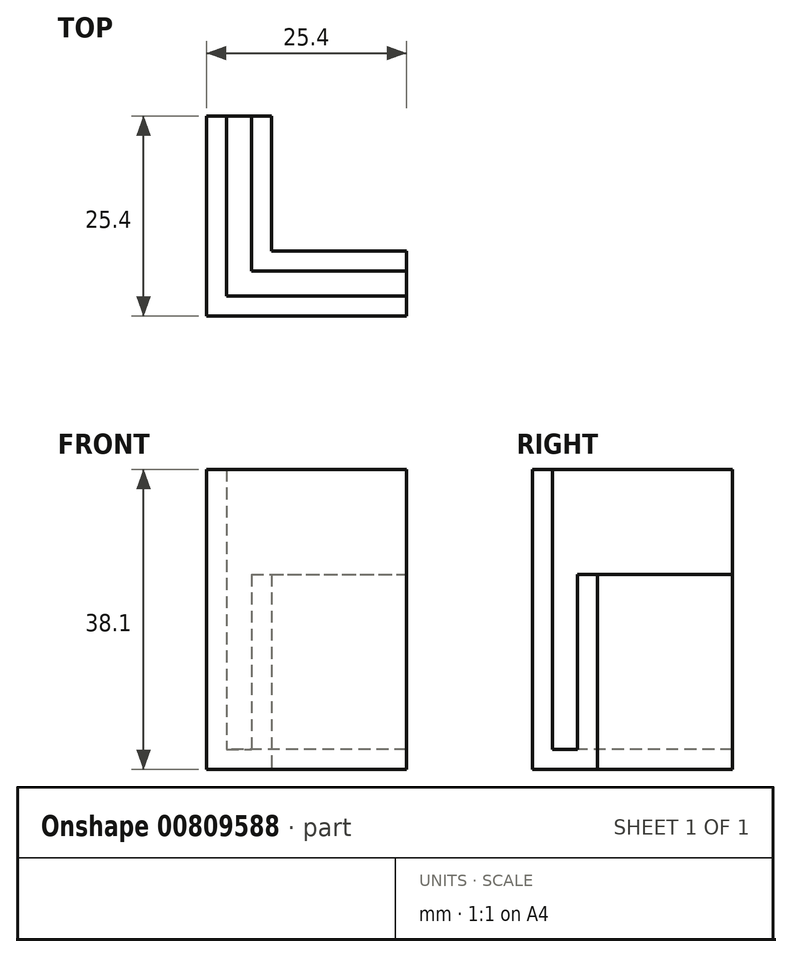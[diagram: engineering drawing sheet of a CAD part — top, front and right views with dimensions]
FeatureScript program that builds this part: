
annotation { "Feature Type Name" : "Feature", "Feature Type Description" : "" }
export const myFeature = defineFeature(function(context is Context, id is Id, definition is map)
    precondition{}
    {
        {
            var Q0;
            Q0=qCreatedBy(makeId("Top.planeOp"),FACE);
            var sketch = newSketch(context, id + "F0", { "sketchPlane" : qUnion([Q0])});
            skLineSegment(sketch, "E0.bottom", {"start": v(0, 0) * mm, "end": v(2.54, 0) * mm});
            skLineSegment(sketch, "E0.top", {"start": v(0, 25.4) * mm, "end": v(2.54, 25.4) * mm});
            skLineSegment(sketch, "E0.left", {"start": v(0, 0) * mm, "end": v(0, 25.4) * mm});
            skLineSegment(sketch, "E0.right", {"start": v(2.54, 0) * mm, "end": v(2.54, 25.4) * mm});
            skLineSegment(sketch, "E1.bottom", {"start": v(0, 0) * mm, "end": v(25.4, 0) * mm});
            skLineSegment(sketch, "E1.top", {"start": v(0, 2.54) * mm, "end": v(25.4, 2.54) * mm});
            skLineSegment(sketch, "E1.left", {"start": v(0, 0) * mm, "end": v(0, 2.54) * mm});
            skLineSegment(sketch, "E1.right", {"start": v(25.4, 0) * mm, "end": v(25.4, 2.54) * mm});
            skLineSegment(sketch, "E2.bottom", {"start": v(0, 0) * mm, "end": v(5.72, 0) * mm});
            skLineSegment(sketch, "E2.top", {"start": v(0, 25.4) * mm, "end": v(5.71, 25.4) * mm});
            skLineSegment(sketch, "E2.right", {"start": v(5.72, 0) * mm, "end": v(5.71, 25.4) * mm});
            skLineSegment(sketch, "E3.bottom", {"start": v(0, 0) * mm, "end": v(8.25, 0) * mm});
            skLineSegment(sketch, "E3.top", {"start": v(0, 25.4) * mm, "end": v(8.25, 25.4) * mm});
            skLineSegment(sketch, "E3.right", {"start": v(8.26, 0) * mm, "end": v(8.25, 25.4) * mm});
            skLineSegment(sketch, "E4.top", {"start": v(0, 5.71) * mm, "end": v(25.4, 5.71) * mm});
            skLineSegment(sketch, "E4.left", {"start": v(0, 0) * mm, "end": v(0, 5.71) * mm});
            skLineSegment(sketch, "E4.right", {"start": v(25.4, 0) * mm, "end": v(25.4, 5.71) * mm});
            skLineSegment(sketch, "E5.top", {"start": v(0, 8.25) * mm, "end": v(25.4, 8.25) * mm});
            skLineSegment(sketch, "E5.left", {"start": v(0, 0) * mm, "end": v(0, 8.25) * mm});
            skLineSegment(sketch, "E5.right", {"start": v(25.4, 0) * mm, "end": v(25.4, 8.25) * mm});
            skSolve(sketch);
        }
        {
            var Q0;
            {var subQ0=sQuery(id+"F0.wireOp",EDGE,"E0.top");Q0=makeQuery(id+"F0.imprint","IMPRINT",FACE,{"disambiguationData":[TD([[makeQuery(id+"F0.imprint","IMPRINT",EDGE,{"derivedFrom":subQ0}),-1.0]])]});}
            var Q1;
            {var subQ0=sQuery(id+"F0.wireOp",EDGE,"E2.top");Q1=makeQuery(id+"F0.imprint","IMPRINT",FACE,{"disambiguationData":[TD([[makeQuery(id+"F0.imprint","IMPRINT",EDGE,{"derivedFrom":subQ0}),-1.0]])]});}
            var Q2;
            {var subQ0=sQuery(id+"F0.wireOp",EDGE,"E3.top");Q2=makeQuery(id+"F0.imprint","IMPRINT",FACE,{"disambiguationData":[TD([[makeQuery(id+"F0.imprint","IMPRINT",EDGE,{"derivedFrom":subQ0}),-1.0]])]});}
            var Q3;
            {var subQ0=sQuery(id+"F0.wireOp",EDGE,"E5.top");var subQ1=sQuery(id+"F0.wireOp",EDGE,"E0.left");var subQ2=makeQuery(id+"F0.imprint","INTERSECT",VERTEX,{"derivedFrom":[subQ1,subQ0]});Q3=makeQuery(id+"F0.imprint","IMPRINT",FACE,{"disambiguationData":[TD([[makeQuery(id+"F0.imprint","IMPRINT",EDGE,{"disambiguationData":[TD([[subQ2,1.0]])],"derivedFrom":subQ1}),-1.0]])]});}
            var Q4;
            {var subQ0=sQuery(id+"F0.wireOp",EDGE,"E1.top");var subQ1=sQuery(id+"F0.wireOp",EDGE,"E0.left");var subQ2=makeQuery(id+"F0.imprint","INTERSECT",VERTEX,{"derivedFrom":[subQ1,subQ0]});Q4=makeQuery(id+"F0.imprint","IMPRINT",FACE,{"disambiguationData":[TD([[makeQuery(id+"F0.imprint","IMPRINT",EDGE,{"disambiguationData":[TD([[subQ2,-1.0]])],"derivedFrom":subQ1}),-1.0]])]});}
            var Q5;
            {var subQ0=sQuery(id+"F0.wireOp",EDGE,"E0.bottom");Q5=makeQuery(id+"F0.imprint","IMPRINT",FACE,{"disambiguationData":[TD([[makeQuery(id+"F0.imprint","IMPRINT",EDGE,{"derivedFrom":subQ0}),1.0]])]});}
            var Q6;
            {var subQ1=sQuery(id+"F0.wireOp",EDGE,"E0.right");var subQ3=sQuery(id+"F0.wireOp",EDGE,"E1.top");var subQ4=makeQuery(id+"F0.imprint","INTERSECT",VERTEX,{"derivedFrom":[subQ1,subQ3]});Q6=makeQuery(id+"F0.imprint","IMPRINT",FACE,{"disambiguationData":[TD([[makeQuery(id+"F0.imprint","IMPRINT",EDGE,{"disambiguationData":[TD([[subQ4,-1.0]])],"derivedFrom":subQ3}),-1.0]])]});}
            var Q7;
            {var subQ0=sQuery(id+"F0.wireOp",EDGE,"E1.top");var subQ1=sQuery(id+"F0.wireOp",EDGE,"E0.right");var subQ2=makeQuery(id+"F0.imprint","INTERSECT",VERTEX,{"derivedFrom":[subQ1,subQ0]});Q7=makeQuery(id+"F0.imprint","IMPRINT",FACE,{"disambiguationData":[TD([[makeQuery(id+"F0.imprint","IMPRINT",EDGE,{"disambiguationData":[TD([[subQ2,-1.0]])],"derivedFrom":subQ1}),-1.0]])]});}
            var Q8;
            {var subQ0=sQuery(id+"F0.wireOp",EDGE,"E5.top");var subQ1=sQuery(id+"F0.wireOp",EDGE,"E0.right");var subQ2=makeQuery(id+"F0.imprint","INTERSECT",VERTEX,{"derivedFrom":[subQ1,subQ0]});Q8=makeQuery(id+"F0.imprint","IMPRINT",FACE,{"disambiguationData":[TD([[makeQuery(id+"F0.imprint","IMPRINT",EDGE,{"disambiguationData":[TD([[subQ2,1.0]])],"derivedFrom":subQ1}),-1.0]])]});}
            var Q9;
            {var subQ0=sQuery(id+"F0.wireOp",EDGE,"E3.right");var subQ1=sQuery(id+"F0.wireOp",EDGE,"E1.top");var subQ2=makeQuery(id+"F0.imprint","INTERSECT",VERTEX,{"derivedFrom":[subQ1,subQ0]});Q9=makeQuery(id+"F0.imprint","IMPRINT",FACE,{"disambiguationData":[TD([[makeQuery(id+"F0.imprint","IMPRINT",EDGE,{"disambiguationData":[TD([[subQ2,1.0]])],"derivedFrom":subQ1}),1.0]])]});}
            var Q10;
            {var subQ0=sQuery(id+"F0.wireOp",EDGE,"E5.top");var subQ1=sQuery(id+"F0.wireOp",EDGE,"E2.right");var subQ2=makeQuery(id+"F0.imprint","INTERSECT",VERTEX,{"derivedFrom":[subQ1,subQ0]});Q10=makeQuery(id+"F0.imprint","IMPRINT",FACE,{"disambiguationData":[TD([[makeQuery(id+"F0.imprint","IMPRINT",EDGE,{"disambiguationData":[TD([[subQ2,1.0]])],"derivedFrom":subQ1}),-1.0]])]});}
            var Q11;
            {var subQ0=sQuery(id+"F0.wireOp",EDGE,"E3.right");var subQ1=sQuery(id+"F0.wireOp",EDGE,"E1.bottom");var subQ2=makeQuery(id+"F0.imprint","INTERSECT",VERTEX,{"derivedFrom":[subQ1,subQ0]});Q11=makeQuery(id+"F0.imprint","IMPRINT",FACE,{"disambiguationData":[TD([[makeQuery(id+"F0.imprint","IMPRINT",EDGE,{"disambiguationData":[TD([[subQ2,1.0]])],"derivedFrom":subQ1}),1.0]])]});}
            var Q12;
            {var subQ3=sQuery(id+"F0.wireOp",EDGE,"E1.right");Q12=makeQuery(id+"F0.imprint","IMPRINT",FACE,{"disambiguationData":[TD([[makeQuery(id+"F0.imprint","IMPRINT",EDGE,{"derivedFrom":subQ3}),1.0]])]});}
            var Q13;
            {var subQ3=sQuery(id+"F0.wireOp",EDGE,"E4.right");Q13=makeQuery(id+"F0.imprint","IMPRINT",FACE,{"disambiguationData":[TD([[makeQuery(id+"F0.imprint","IMPRINT",EDGE,{"derivedFrom":subQ3}),1.0]])]});}
            var Q14;
            {var subQ5=sQuery(id+"F0.wireOp",EDGE,"E5.right");Q14=makeQuery(id+"F0.imprint","IMPRINT",FACE,{"disambiguationData":[TD([[makeQuery(id+"F0.imprint","IMPRINT",EDGE,{"derivedFrom":subQ5}),1.0]])]});}
            extrude(context, id + "F1", {"entities" : qUnion([Q0, Q1, Q2, Q3, Q4, Q5, Q6, Q7, Q8, Q9, Q10, Q11, Q12, Q13, Q14]), "depth" : 2.54 * mm, "offsetDistance" : 25.4 * mm});
        }
        {
            var Q0;
            {var subQ0=sQuery(id+"F0.wireOp",EDGE,"E3.top");Q0=makeQuery(id+"F0.imprint","IMPRINT",FACE,{"disambiguationData":[TD([[makeQuery(id+"F0.imprint","IMPRINT",EDGE,{"derivedFrom":subQ0}),-1.0]])]});}
            var Q1;
            {var subQ0=sQuery(id+"F0.wireOp",EDGE,"E5.top");var subQ1=sQuery(id+"F0.wireOp",EDGE,"E2.right");var subQ2=makeQuery(id+"F0.imprint","INTERSECT",VERTEX,{"derivedFrom":[subQ1,subQ0]});Q1=makeQuery(id+"F0.imprint","IMPRINT",FACE,{"disambiguationData":[TD([[makeQuery(id+"F0.imprint","IMPRINT",EDGE,{"disambiguationData":[TD([[subQ2,1.0]])],"derivedFrom":subQ1}),-1.0]])]});}
            var Q2;
            {var subQ5=sQuery(id+"F0.wireOp",EDGE,"E5.right");Q2=makeQuery(id+"F0.imprint","IMPRINT",FACE,{"disambiguationData":[TD([[makeQuery(id+"F0.imprint","IMPRINT",EDGE,{"derivedFrom":subQ5}),1.0]])]});}
            extrude(context, id + "F2", {"entities" : qUnion([Q0, Q1, Q2]), "operationType" : NewBodyOperationType.ADD, "depth" : 24.77 * mm, "offsetDistance" : 25.4 * mm});
        }
        {
            var Q0;
            {var subQ0=sQuery(id+"F0.wireOp",EDGE,"E0.top");Q0=makeQuery(id+"F0.imprint","IMPRINT",FACE,{"disambiguationData":[TD([[makeQuery(id+"F0.imprint","IMPRINT",EDGE,{"derivedFrom":subQ0}),-1.0]])]});}
            var Q1;
            {var subQ0=sQuery(id+"F0.wireOp",EDGE,"E5.top");var subQ1=sQuery(id+"F0.wireOp",EDGE,"E0.left");var subQ2=makeQuery(id+"F0.imprint","INTERSECT",VERTEX,{"derivedFrom":[subQ1,subQ0]});Q1=makeQuery(id+"F0.imprint","IMPRINT",FACE,{"disambiguationData":[TD([[makeQuery(id+"F0.imprint","IMPRINT",EDGE,{"disambiguationData":[TD([[subQ2,1.0]])],"derivedFrom":subQ1}),-1.0]])]});}
            var Q2;
            {var subQ0=sQuery(id+"F0.wireOp",EDGE,"E1.top");var subQ1=sQuery(id+"F0.wireOp",EDGE,"E0.left");var subQ2=makeQuery(id+"F0.imprint","INTERSECT",VERTEX,{"derivedFrom":[subQ1,subQ0]});Q2=makeQuery(id+"F0.imprint","IMPRINT",FACE,{"disambiguationData":[TD([[makeQuery(id+"F0.imprint","IMPRINT",EDGE,{"disambiguationData":[TD([[subQ2,-1.0]])],"derivedFrom":subQ1}),-1.0]])]});}
            var Q3;
            {var subQ0=sQuery(id+"F0.wireOp",EDGE,"E0.bottom");Q3=makeQuery(id+"F0.imprint","IMPRINT",FACE,{"disambiguationData":[TD([[makeQuery(id+"F0.imprint","IMPRINT",EDGE,{"derivedFrom":subQ0}),1.0]])]});}
            var Q4;
            {var subQ1=sQuery(id+"F0.wireOp",EDGE,"E0.right");var subQ3=sQuery(id+"F0.wireOp",EDGE,"E1.top");var subQ4=makeQuery(id+"F0.imprint","INTERSECT",VERTEX,{"derivedFrom":[subQ1,subQ3]});Q4=makeQuery(id+"F0.imprint","IMPRINT",FACE,{"disambiguationData":[TD([[makeQuery(id+"F0.imprint","IMPRINT",EDGE,{"disambiguationData":[TD([[subQ4,-1.0]])],"derivedFrom":subQ3}),-1.0]])]});}
            var Q5;
            {var subQ0=sQuery(id+"F0.wireOp",EDGE,"E3.right");var subQ1=sQuery(id+"F0.wireOp",EDGE,"E1.bottom");var subQ2=makeQuery(id+"F0.imprint","INTERSECT",VERTEX,{"derivedFrom":[subQ1,subQ0]});Q5=makeQuery(id+"F0.imprint","IMPRINT",FACE,{"disambiguationData":[TD([[makeQuery(id+"F0.imprint","IMPRINT",EDGE,{"disambiguationData":[TD([[subQ2,1.0]])],"derivedFrom":subQ1}),1.0]])]});}
            var Q6;
            {var subQ3=sQuery(id+"F0.wireOp",EDGE,"E1.right");Q6=makeQuery(id+"F0.imprint","IMPRINT",FACE,{"disambiguationData":[TD([[makeQuery(id+"F0.imprint","IMPRINT",EDGE,{"derivedFrom":subQ3}),1.0]])]});}
            extrude(context, id + "F3", {"entities" : qUnion([Q0, Q1, Q2, Q3, Q4, Q5, Q6]), "operationType" : NewBodyOperationType.ADD, "depth" : 38.1 * mm, "offsetDistance" : 25.4 * mm});
        }
    });
